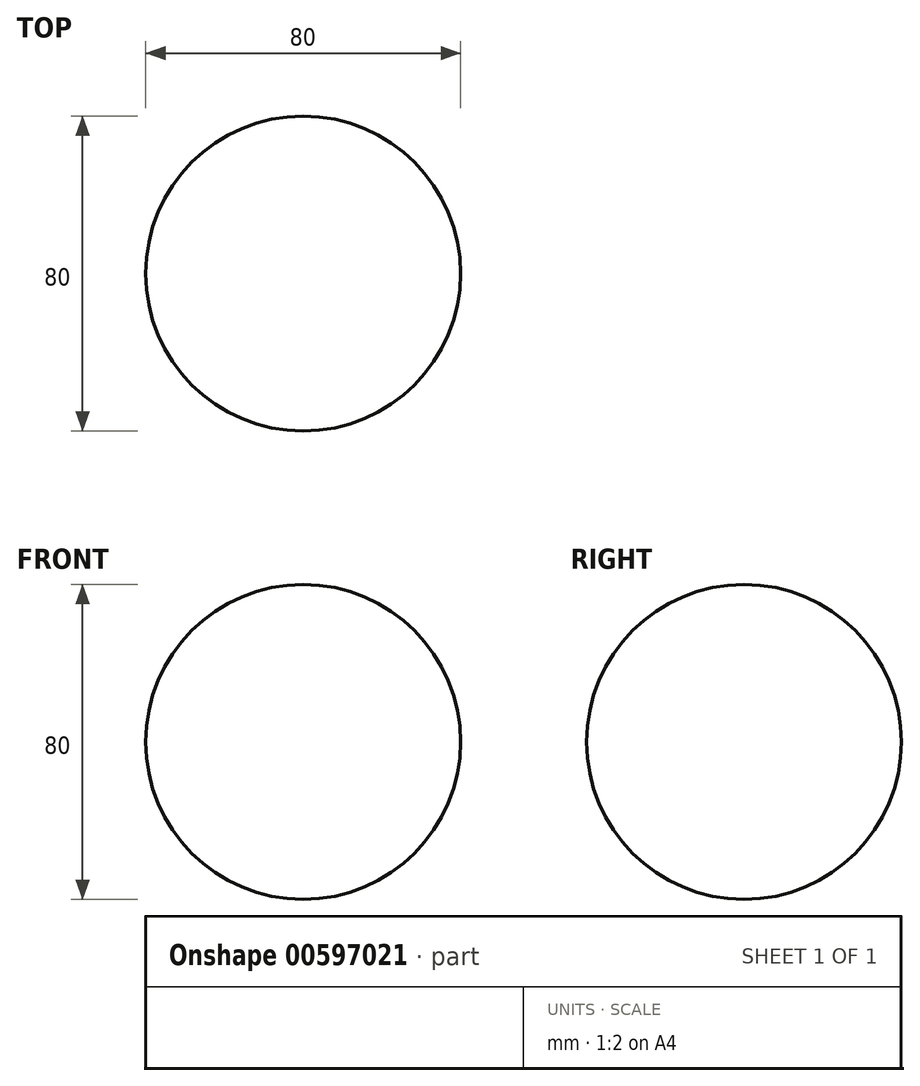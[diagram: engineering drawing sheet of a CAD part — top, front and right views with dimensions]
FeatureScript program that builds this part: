
annotation { "Feature Type Name" : "Feature", "Feature Type Description" : "" }
export const myFeature = defineFeature(function(context is Context, id is Id, definition is map)
    precondition{}
    {
        {
            var Q0;
            Q0=qCreatedBy(makeId("Front.planeOp"),FACE);
            var sketch = newSketch(context, id + "F0", { "sketchPlane" : qUnion([Q0])});
            skArc(sketch, "E0", {"start": v(0, -40) * mm, "mid": v(40, 0) * mm, "end": v(0, 40) * mm});
            skLineSegment(sketch, "E1", {"start": v(0, 40) * mm, "end": v(0, -40) * mm});
            skSolve(sketch);
        }
        {
            var Q0;
            Q0=qCreatedBy(makeId("Front.planeOp"),FACE);
            var sketch = newSketch(context, id + "F1", { "sketchPlane" : qUnion([Q0])});
            skLineSegment(sketch, "E2", {"start": v(0, 39.8) * mm, "end": v(0, -39.8) * mm});
            skSolve(sketch);
        }
        {
            var Q0;
            Q0=qSketchRegion(id+"F0",true);
            var Q1;
            Q1=sQuery(id+"F1.wireOp",EDGE,"E2");
            revolve(context, id + "F2", {"entities" : qUnion([Q0]), "axis" : qUnion([Q1]), "revolveType" : RevolveType.FULL});
        }
    });
